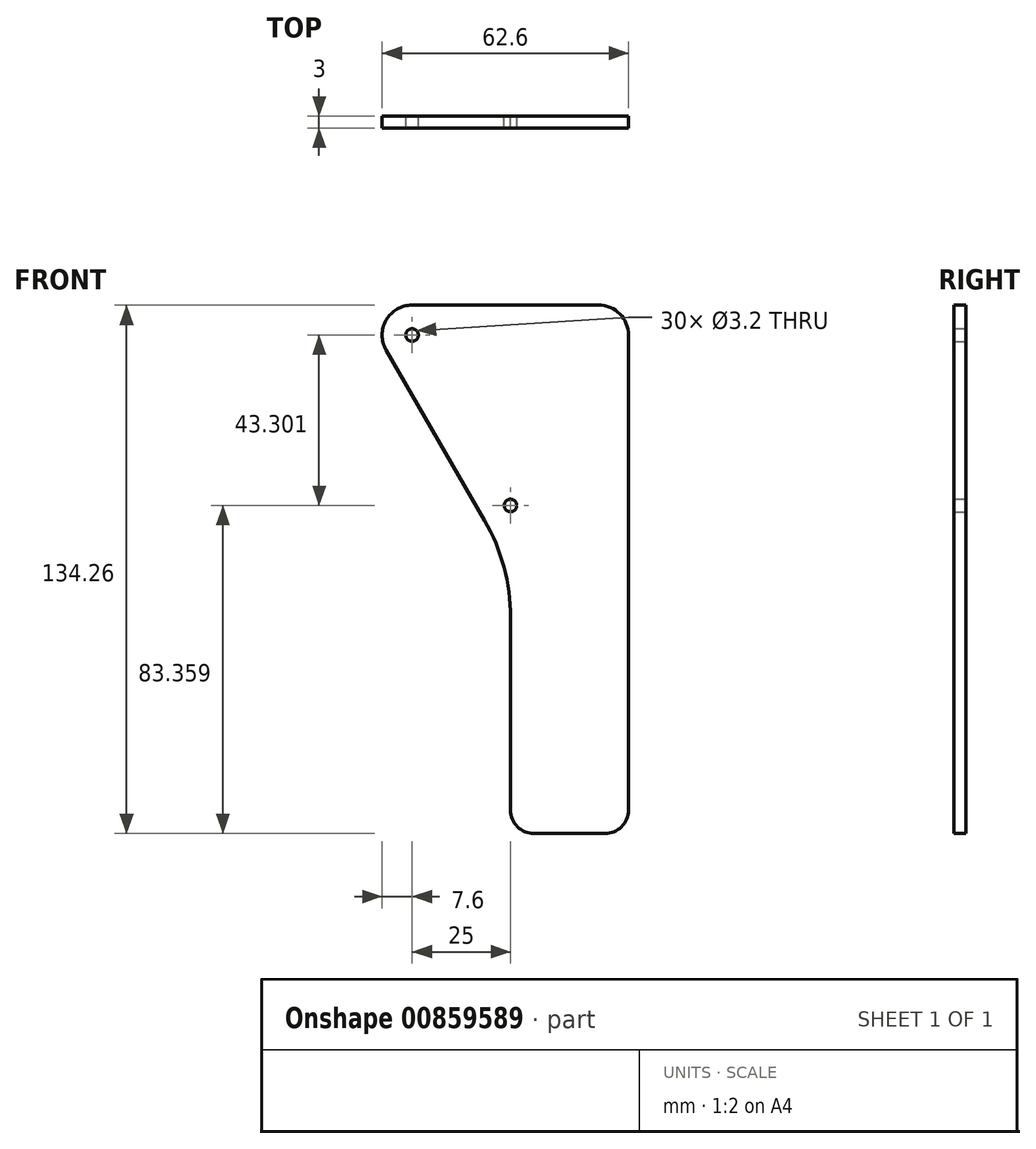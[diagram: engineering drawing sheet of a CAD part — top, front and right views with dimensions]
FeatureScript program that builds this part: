
annotation { "Feature Type Name" : "Feature", "Feature Type Description" : "" }
export const myFeature = defineFeature(function(context is Context, id is Id, definition is map)
    precondition{}
    {
        {
            var Q0;
            Q0=qCreatedBy(makeId("Front.planeOp"),FACE);
            var sketch = newSketch(context, id + "F0", { "sketchPlane" : qUnion([Q0])});
            skCircle(sketch, "E0", {"center": v(0, 0) * mm, "radius": 1.6 * mm});
            skCircle(sketch, "E1", {"center": v(25, -43.3) * mm, "radius": 1.6 * mm});
            skLineSegment(sketch, "E2", {"start": v(0, 0) * mm, "end": v(25, -43.3) * mm, "construction": true});
            skLineSegment(sketch, "E3", {"start": v(0, 0) * mm, "end": v(0, -43.3) * mm, "construction": true});
            skArc(sketch, "E4", {"start": v(0, 7.6) * mm, "mid": v(-6.58, 3.8) * mm, "end": v(-6.58, -3.8) * mm});
            skLineSegment(sketch, "E5", {"start": v(-6.58, -3.8) * mm, "end": v(18.42, -47.1) * mm});
            skArc(sketch, "E6", {"start": v(18.42, -47.1) * mm, "mid": v(23.33, -58.95) * mm, "end": v(25, -71.66) * mm});
            skLineSegment(sketch, "E7", {"start": v(0, 7.6) * mm, "end": v(47.4, 7.6) * mm});
            skLineSegment(sketch, "E8", {"start": v(25, -71.66) * mm, "end": v(25, -120.66) * mm});
            skLineSegment(sketch, "E9", {"start": v(31, -126.66) * mm, "end": v(49, -126.66) * mm});
            skLineSegment(sketch, "E10", {"start": v(55, -120.66) * mm, "end": v(55, 0) * mm});
            skArc(sketch, "E11", {"start": v(55, 0) * mm, "mid": v(52.77, 5.37) * mm, "end": v(47.4, 7.6) * mm});
            skLineSegment(sketch, "E12", {"start": v(18.42, -47.1) * mm, "end": v(25, -43.3) * mm, "construction": true});
            skPoint(sketch, "E13.visualSharp", {"position": v(25, -126.66) * mm});
            skArc(sketch, "E13.filletArc", {"start": v(25, -120.66) * mm, "mid": v(26.76, -124.9) * mm, "end": v(31, -126.66) * mm});
            skPoint(sketch, "E14.visualSharp", {"position": v(55, -126.66) * mm});
            skArc(sketch, "E14.filletArc", {"start": v(49, -126.66) * mm, "mid": v(53.24, -124.9) * mm, "end": v(55, -120.66) * mm});
            skSolve(sketch);
        }
        {
            var Q0;
            Q0=makeQuery(id+"F0.imprint","IMPRINT",FACE,{"disambiguationData":[TD([[makeQuery(id+"F0.imprint","IMPRINT",EDGE,{"derivedFrom":sQuery(id+"F0.wireOp",EDGE,"E0")}),-1.0]])]});
            extrude(context, id + "F1", {"entities" : qUnion([Q0]), "depth" : 3 * mm, "offsetDistance" : 25 * mm});
        }
    });
